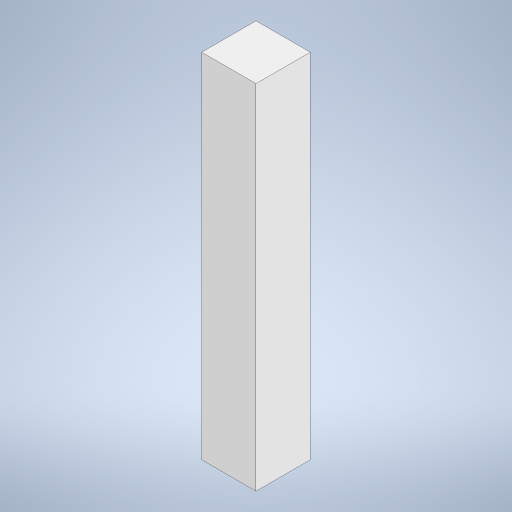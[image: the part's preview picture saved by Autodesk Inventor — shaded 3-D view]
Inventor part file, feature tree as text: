
AUTODESK INVENTOR PART (.ipt)
format: ipt  version: 2024 (Build 280153000, 153)  size: 224,256 bytes
history: native  units: in
note: dims shown in document units (in); Inventor stores cm internally (conversion verified against a paired STEP export)
features: extrude x1, sketch x1
ambient origin geometry x8: Origin, YZ Plane, XZ Plane, XY Plane, X Axis, Y Axis, Z Axis, Center Point
bodies: Solid1 (feature_tree)
feature tree (2):
  extrude  "Extrusion1"  Depth=12.0in
  sketch  "Sketch1"  dims[d2=12.0in d3=12.0in d4=78.0in d5=0.0in]
